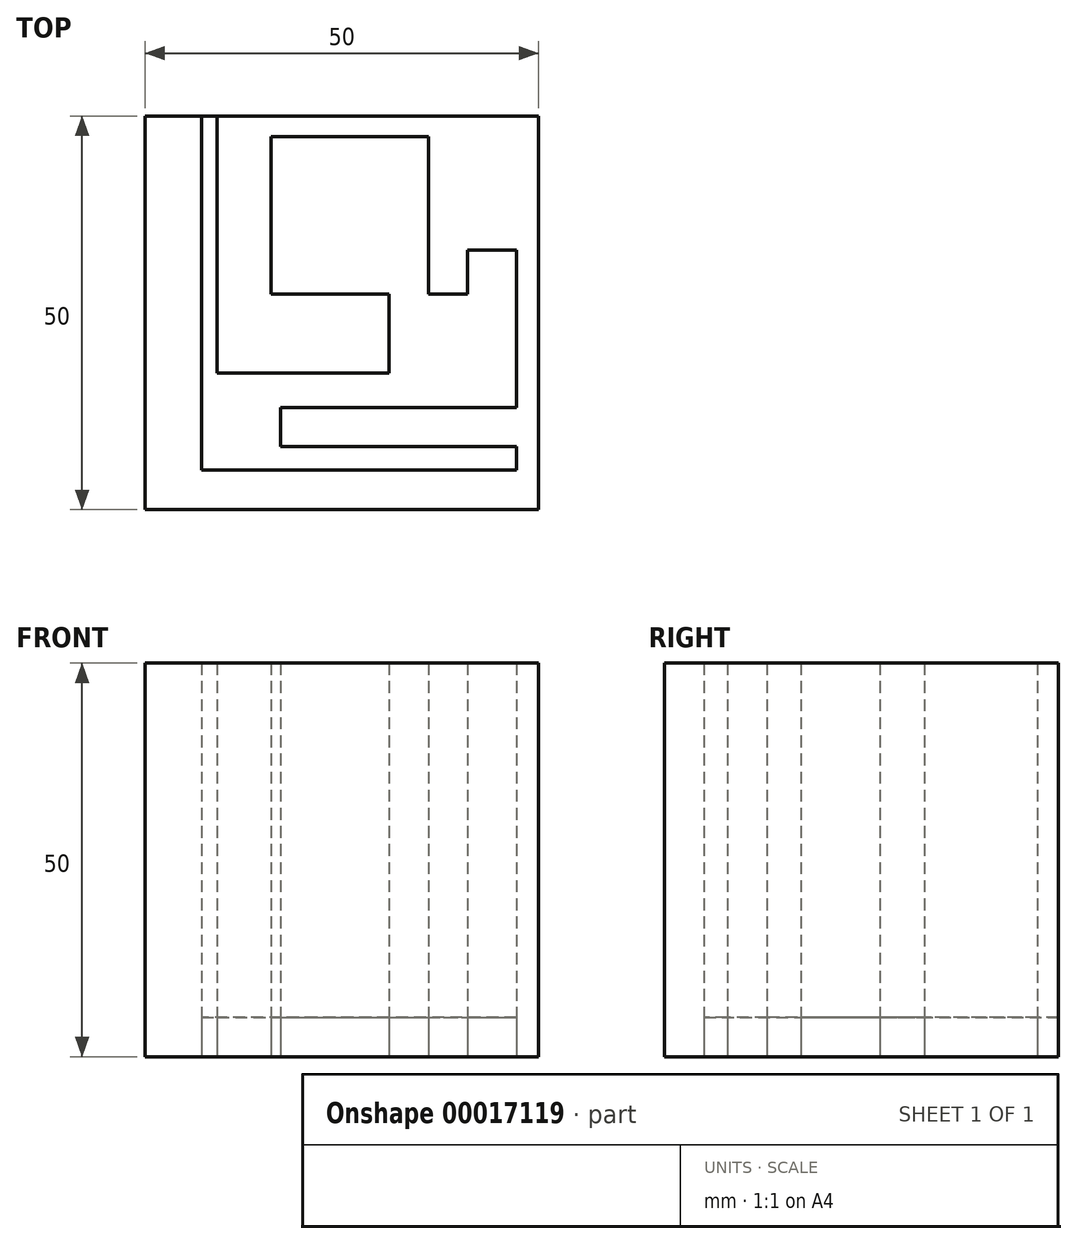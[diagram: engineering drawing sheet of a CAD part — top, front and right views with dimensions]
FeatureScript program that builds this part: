
annotation { "Feature Type Name" : "Feature", "Feature Type Description" : "" }
export const myFeature = defineFeature(function(context is Context, id is Id, definition is map)
    precondition{}
    {
        {
            var Q0;
            Q0=qCreatedBy(makeId("Top.planeOp"),FACE);
            var sketch = newSketch(context, id + "F0", { "sketchPlane" : qUnion([Q0])});
            skLineSegment(sketch, "E0.bottom", {"start": v(-47.2, 42.02) * mm, "end": v(2.8, 42.02) * mm});
            skLineSegment(sketch, "E0.top", {"start": v(-47.2, -7.98) * mm, "end": v(2.8, -7.98) * mm});
            skLineSegment(sketch, "E0.left", {"start": v(-47.2, 42.02) * mm, "end": v(-47.2, -7.98) * mm});
            skLineSegment(sketch, "E0.right", {"start": v(2.8, 42.02) * mm, "end": v(2.8, -7.98) * mm});
            skLineSegment(sketch, "E1", {"start": v(-38.01, 42.02) * mm, "end": v(-38.01, 9.33) * mm});
            skLineSegment(sketch, "E2", {"start": v(-38.01, 9.33) * mm, "end": v(-16.21, 9.33) * mm});
            skLineSegment(sketch, "E3", {"start": v(-16.21, 9.33) * mm, "end": v(-16.21, 19.39) * mm});
            skLineSegment(sketch, "E4", {"start": v(-16.21, 19.39) * mm, "end": v(-31.21, 19.39) * mm});
            skLineSegment(sketch, "E5", {"start": v(-31.21, 19.39) * mm, "end": v(-31.21, 39.39) * mm});
            skLineSegment(sketch, "E6", {"start": v(-31.21, 39.39) * mm, "end": v(-11.21, 39.39) * mm});
            skLineSegment(sketch, "E7", {"start": v(-11.21, 39.39) * mm, "end": v(-11.21, 19.39) * mm});
            skLineSegment(sketch, "E8", {"start": v(-11.21, 19.39) * mm, "end": v(-6.21, 19.39) * mm});
            skLineSegment(sketch, "E9", {"start": v(-6.21, 19.39) * mm, "end": v(-6.21, 25) * mm});
            skLineSegment(sketch, "E10", {"start": v(-6.21, 25) * mm, "end": v(0, 25) * mm});
            skLineSegment(sketch, "E11", {"start": v(0, 25) * mm, "end": v(0, 5) * mm});
            skLineSegment(sketch, "E12", {"start": v(0, 5) * mm, "end": v(-30, 5) * mm});
            skLineSegment(sketch, "E13", {"start": v(-30, 5) * mm, "end": v(-30, 0) * mm});
            skLineSegment(sketch, "E14", {"start": v(-30, 0) * mm, "end": v(0, 0) * mm});
            skLineSegment(sketch, "E15", {"start": v(0, 0) * mm, "end": v(0, -2.98) * mm});
            skLineSegment(sketch, "E16", {"start": v(0, -2.98) * mm, "end": v(-40, -2.98) * mm});
            skLineSegment(sketch, "E17", {"start": v(-40, -2.98) * mm, "end": v(-40, 42.02) * mm});
            skSolve(sketch);
        }
        {
            var Q0;
            Q0=makeQuery(id+"F0.imprint","IMPRINT",FACE,{"disambiguationData":[TD([[makeQuery(id+"F0.imprint","IMPRINT",EDGE,{"derivedFrom":sQuery(id+"F0.wireOp",EDGE,"E0.top")}),1.0]])]});
            extrude(context, id + "F1", {"entities" : qUnion([Q0]), "depth" : 50 * mm});
        }
        {
            var Q0;
            {var subQ1=sQuery(id+"F0.wireOp",EDGE,"E1");Q0=makeQuery(id+"F0.imprint","IMPRINT",FACE,{"disambiguationData":[TD([[makeQuery(id+"F0.imprint","IMPRINT",EDGE,{"derivedFrom":subQ1}),-1.0]])]});}
            extrude(context, id + "F2", {"entities" : qUnion([Q0]), "depth" : 5 * mm});
        }
    });
